# Revit family: JC KONTAKTER JCK109 FI
name_source: partatom
category: Specialty Equipment
units: mm (PartAtom-declared; Revit-internal decimal feet)

## family parameters
Cut with Voids When Loaded = No
Enable Cutting in Views = Yes
Host = Face
Maintain Annotation Orientation = Yes
Part Type = Normal
Room Calculation Point = No
Round Connector Dimension = Use Diameter
Shared = No

## types (1)
- JCK109
    CE asiakirja = https://jckontakter.se
    Default Elevation = 800 mm  [stored 2.62467 ft]
    Description = Tämä kyynärkytkin on valmistettu iskunkestävästä ABS-muovista ja siinä on litteä painopinta. Tässä mallissa on valkoinen painopinta ja valkoinen kehys. Se on ensisijaisesti suunniteltu sisäkäyttöön, mutta sitä voidaan käyttää myös ulkona, sillä siinä on kosteussuojattu mikrokytkin, jonka IP-luokitus on 67.
    Kansi = ABS 750SW (Valkoinen)
    Kotelo = ABS 750SW (Valkoinen)
    Manufacturer = JC Kontakter
    Mikrokytkimien määrä = 1
    Mikrokytkin = Standar NO IP67
    Model = JCK109
    Nimellisestä nimellisvirrasta = 1mA/4 V DC
    Pienin nimellisvirta = 12V Resistiivinen 6A Induktiivinen L/R 5ms 6A, 24V Resistiivinen 6A Induktiivinen L/R 5ms 5A
    Tekniken tuotekortti = https://www.jckontakter.fi
    Tuotteen paino = 0.216 kg
    URL = https://www.jckontakter.fi
    Valmistusmaa = Ruotsi

note: [stored X ft] marks values corroborated as IEEE doubles in the binary element streams (Revit-internal decimal feet)

## geometry (parser evidence)
native form markers: Sweep x6
no freeform markers — native parametric forms only
